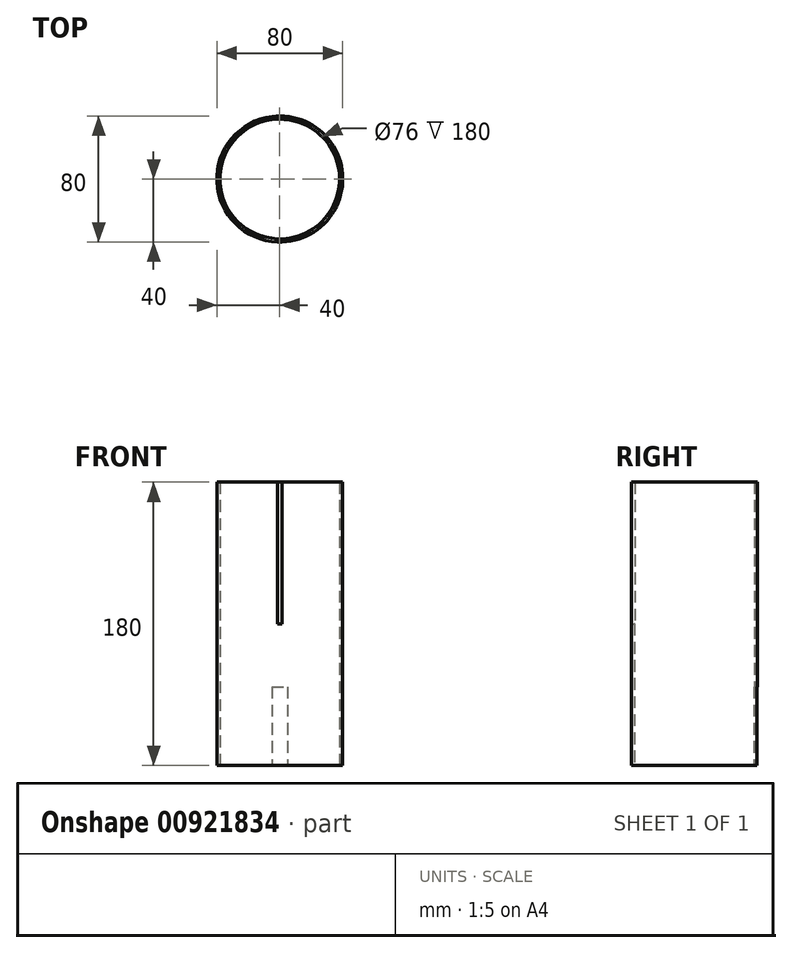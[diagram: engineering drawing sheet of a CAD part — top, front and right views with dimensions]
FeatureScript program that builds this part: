
annotation { "Feature Type Name" : "Feature", "Feature Type Description" : "" }
export const myFeature = defineFeature(function(context is Context, id is Id, definition is map)
    precondition{}
    {
        {
            var Q0;
            Q0=qCreatedBy(makeId("Top.planeOp"),FACE);
            var sketch = newSketch(context, id + "F0", { "sketchPlane" : qUnion([Q0])});
            skCircle(sketch, "E0", {"center": v(0, 0) * mm, "radius": 40 * mm});
            skCircle(sketch, "E1", {"center": v(0, 0) * mm, "radius": 38 * mm});
            skSolve(sketch);
        }
        {
            var Q0;
            Q0 = qSketchRegion(id + "F0", true);
            extrude(context, id + "F1", {"entities" : qUnion([Q0]), "depth" : 180 * mm, "offsetDistance" : 25 * mm});
        }
        {
            var Q0;
            Q0=qCreatedBy(makeId("Front.planeOp"),FACE);
            var sketch = newSketch(context, id + "F2", { "sketchPlane" : qUnion([Q0])});
            skLineSegment(sketch, "E2", {"start": v(0, 63.9) * mm, "end": v(0, 50.14) * mm, "construction": true});
            skLineSegment(sketch, "E3.bottom", {"start": v(-1.5, 90) * mm, "end": v(1.5, 90) * mm});
            skLineSegment(sketch, "E3.top", {"start": v(-1.5, 180) * mm, "end": v(1.5, 180) * mm});
            skLineSegment(sketch, "E3.left", {"start": v(-1.5, 90) * mm, "end": v(-1.5, 180) * mm});
            skLineSegment(sketch, "E3.right", {"start": v(1.5, 90) * mm, "end": v(1.5, 180) * mm});
            skSolve(sketch);
        }
        {
            var Q0;
            Q0 = qSketchRegion(id + "F2", true);
            extrude(context, id + "F3", {"entities" : qUnion([Q0]), "operationType" : NewBodyOperationType.REMOVE, "depth" : 160 * mm, "offsetDistance" : 25 * mm});
        }
        {
            var Q0;
            Q0=qCreatedBy(makeId("Front.planeOp"),FACE);
            var sketch = newSketch(context, id + "F4", { "sketchPlane" : qUnion([Q0])});
            skLineSegment(sketch, "E4.bottom", {"start": v(-5, 50) * mm, "end": v(5, 50) * mm});
            skLineSegment(sketch, "E4.top", {"start": v(-5, 0) * mm, "end": v(5, 0) * mm});
            skLineSegment(sketch, "E4.left", {"start": v(-5, 50) * mm, "end": v(-5, 0) * mm});
            skLineSegment(sketch, "E4.right", {"start": v(5, 50) * mm, "end": v(5, 0) * mm});
            skLineSegment(sketch, "E5", {"start": v(0, -9.3) * mm, "end": v(0, 74.9) * mm, "construction": true});
            skSolve(sketch);
        }
        {
            var Q0;
            Q0 = qSketchRegion(id + "F4", true);
            extrude(context, id + "F5", {"entities" : qUnion([Q0]), "operationType" : NewBodyOperationType.REMOVE, "oppositeDirection" : true, "depth" : 66.8 * mm, "offsetDistance" : 25 * mm});
        }
    });
